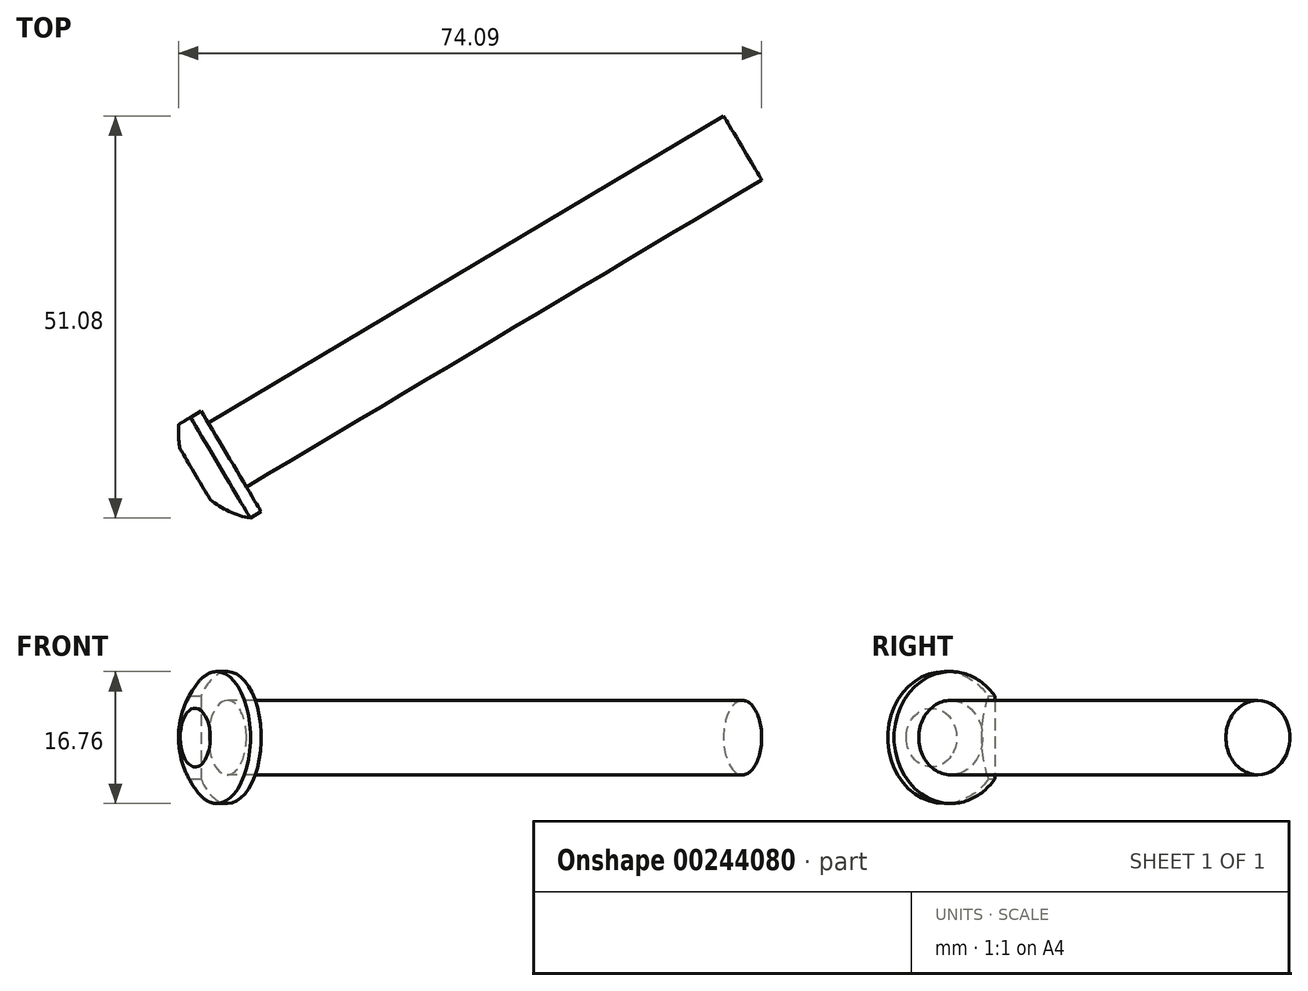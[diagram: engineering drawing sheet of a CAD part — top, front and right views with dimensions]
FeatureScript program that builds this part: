
annotation { "Feature Type Name" : "Feature", "Feature Type Description" : "" }
export const myFeature = defineFeature(function(context is Context, id is Id, definition is map)
    precondition{}
    {
        {
            var Q0;
            Q0=qCreatedBy(makeId("Top.planeOp"),FACE);
            var sketch = newSketch(context, id + "F0", { "sketchPlane" : qUnion([Q0])});
            skArc(sketch, "E0", {"start": v(-64.68, 39.56) * mm, "mid": v(-65.21, 36.77) * mm, "end": v(-65.03, 33.94) * mm});
            skLineSegment(sketch, "E1", {"start": v(-63.31, 40.37) * mm, "end": v(-59.02, 33.17) * mm});
            skLineSegment(sketch, "E2", {"start": v(-65.03, 33.94) * mm, "end": v(-63.11, 30.74) * mm});
            skPoint(sketch, "E3", {"position": v(-59.02, 33.17) * mm});
            skLineSegment(sketch, "E4", {"start": v(-59.02, 33.17) * mm, "end": v(6.43, 72.2) * mm});
            skLineSegment(sketch, "E5", {"start": v(6.43, 72.2) * mm, "end": v(4, 76.25) * mm});
            skLineSegment(sketch, "E6", {"start": v(-61.44, 37.23) * mm, "end": v(4, 76.25) * mm});
            skLineSegment(sketch, "E7", {"start": v(-59.02, 33.17) * mm, "end": v(-63.11, 30.74) * mm});
            skPoint(sketch, "E8.trimOffspring.end.orphan", {"position": v(-54.15, 25) * mm});
            skPoint(sketch, "E8.trimOffspring.start.orphan", {"position": v(-61.2, 27.53) * mm});
            skLineSegment(sketch, "E9", {"start": v(-60.39, 32.36) * mm, "end": v(-64.68, 39.56) * mm});
            skLineSegment(sketch, "E10", {"start": v(-64.68, 39.56) * mm, "end": v(-63.31, 40.37) * mm});
            skPoint(sketch, "E11.orphan", {"position": v(-63.9, 41.36) * mm});
            skSolve(sketch);
        }
        {
            var Q0;
            {var subQ0=sQuery(id+"F0.wireOp",EDGE,"E4");Q0=makeQuery(id+"F0.imprint","IMPRINT",FACE,{"disambiguationData":[TD([[makeQuery(id+"F0.imprint","IMPRINT",EDGE,{"derivedFrom":subQ0}),1.0]])]});}
            var Q1;
            {var subQ0=sQuery(id+"F0.wireOp",EDGE,"E9");Q1=makeQuery(id+"F0.imprint","IMPRINT",FACE,{"disambiguationData":[TD([[makeQuery(id+"F0.imprint","IMPRINT",EDGE,{"derivedFrom":subQ0}),-1.0]])]});}
            var Q2;
            Q2=makeQuery(id+"F0.imprint","IMPRINT",FACE,{"disambiguationData":[TD([[makeQuery(id+"F0.imprint","IMPRINT",EDGE,{"derivedFrom":sQuery(id+"F0.wireOp",EDGE,"E0")}),1.0]])]});
            var Q3;
            Q3=sQuery(id+"F0.wireOp",EDGE,"E4");
            revolve(context, id + "F1", {"entities" : qUnion([Q0, Q1, Q2]), "axis" : qUnion([Q3]), "revolveType" : RevolveType.FULL});
        }
        {
            var Q0;
            Q0=makeQuery(id+"F1.opRevolve","SWEPT_FACE",FACE,{"disambiguationData":[OSD([sQuery(id+"F0.wireOp",EDGE,"E1")])]});
            var sketch = newSketch(context, id + "F2", { "sketchPlane" : qUnion([Q0])});
            skLineSegment(sketch, "E12", {"start": v(65.23, 5.27) * mm, "end": v(65.23, -5.27) * mm});
            skArc(sketch, "E13", {"start": v(65.23, -5.27) * mm, "mid": v(67.1, 0) * mm, "end": v(65.23, 5.27) * mm});
            skSolve(sketch);
        }
        {
            var Q0;
            Q0 = qSketchRegion(id + "F2", true);
            extrude(context, id + "F3", {"entities" : qUnion([Q0]), "operationType" : NewBodyOperationType.REMOVE, "oppositeDirection" : true, "depth" : 25.4 * mm});
        }
    });
